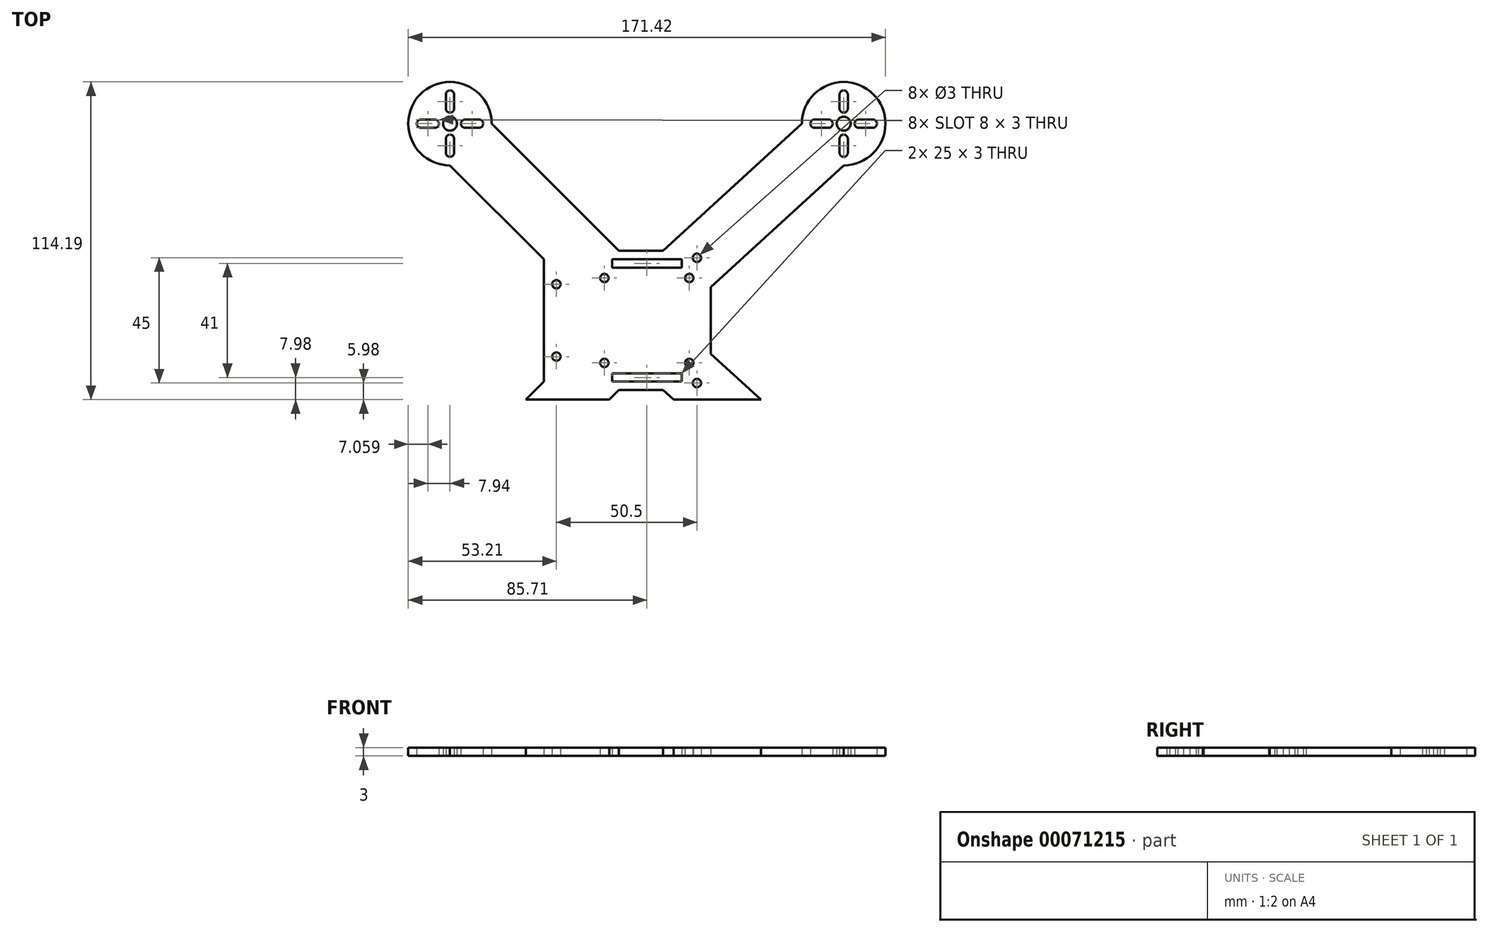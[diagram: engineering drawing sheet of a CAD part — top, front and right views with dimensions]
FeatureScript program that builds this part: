
annotation { "Feature Type Name" : "Feature", "Feature Type Description" : "" }
export const myFeature = defineFeature(function(context is Context, id is Id, definition is map)
    precondition{}
    {
        {
            var Q0;
            Q0=qCreatedBy(makeId("Top.planeOp"),FACE);
            var sketch = newSketch(context, id + "F0", { "sketchPlane" : qUnion([Q0])});
            skLineSegment(sketch, "E0.rect.left", {"start": v(70.71, -70.71) * mm, "end": v(70.71, 70.71) * mm, "construction": true});
            skLineSegment(sketch, "E0.rect.right", {"start": v(-70.71, -70.71) * mm, "end": v(-70.71, 70.71) * mm, "construction": true});
            skPoint(sketch, "E0.rect.middle", {"position": v(0, 0) * mm});
            skArc(sketch, "E1", {"start": v(-55.71, 70.71) * mm, "mid": v(-81.32, 81.32) * mm, "end": v(-70.71, 55.71) * mm});
            skLineSegment(sketch, "E2", {"start": v(70.71, 70.71) * mm, "end": v(-70.71, -70.71) * mm, "construction": true});
            skLineSegment(sketch, "E3", {"start": v(70.71, -70.71) * mm, "end": v(-70.71, 70.71) * mm, "construction": true});
            skCircle(sketch, "E4", {"center": v(-70.71, 70.71) * mm, "radius": 2.5 * mm});
            skLineSegment(sketch, "E5.rect.left", {"start": v(-69.21, 76.15) * mm, "end": v(-69.21, 81.15) * mm});
            skLineSegment(sketch, "E5.rect.right", {"start": v(-72.21, 76.15) * mm, "end": v(-72.21, 81.15) * mm});
            skArc(sketch, "E6", {"start": v(-69.21, 81.15) * mm, "mid": v(-70.71, 82.65) * mm, "end": v(-72.21, 81.15) * mm});
            skArc(sketch, "E7", {"start": v(-72.21, 76.15) * mm, "mid": v(-70.71, 74.65) * mm, "end": v(-69.21, 76.15) * mm});
            skLineSegment(sketch, "E8", {"start": v(-70.71, 70.71) * mm, "end": v(70.71, 70.71) * mm, "construction": true});
            skCircle(sketch, "E9.MirrorC", {"center": v(70.71, 70.71) * mm, "radius": 2.5 * mm});
            skArc(sketch, "E10.MirrorC", {"start": v(55.71, 70.71) * mm, "mid": v(81.32, 81.32) * mm, "end": v(70.71, 55.71) * mm});
            skLineSegment(sketch, "E11.rect.bottom", {"start": v(18, 18) * mm, "end": v(-18, 18) * mm, "construction": true});
            skLineSegment(sketch, "E11.rect.top", {"start": v(18, -18) * mm, "end": v(-18, -18) * mm, "construction": true});
            skLineSegment(sketch, "E11.rect.left", {"start": v(18, 18) * mm, "end": v(18, -18) * mm, "construction": true});
            skLineSegment(sketch, "E11.rect.right", {"start": v(-18, 18) * mm, "end": v(-18, -18) * mm, "construction": true});
            skLineSegment(sketch, "E12.rect.top", {"start": v(-10, 25) * mm, "end": v(5.83, 25) * mm});
            skLineSegment(sketch, "E12.rect.left", {"start": v(-37, -22) * mm, "end": v(-37, 22) * mm});
            skCircle(sketch, "E13", {"center": v(18, -22.5) * mm, "radius": 1.5 * mm});
            skCircle(sketch, "E14.MirrorC", {"center": v(18, 22.5) * mm, "radius": 1.5 * mm});
            skLineSegment(sketch, "E15.MirrorCS", {"start": v(70.71, 55.71) * mm, "end": v(23, 12) * mm});
            skLineSegment(sketch, "E16.MirrorCS", {"start": v(55.71, 70.71) * mm, "end": v(5.83, 25) * mm});
            skLineSegment(sketch, "E17.MirrorCS", {"start": v(-70.71, 55.71) * mm, "end": v(-37, 22) * mm});
            skLineSegment(sketch, "E18.MirrorCS", {"start": v(-55.71, 70.71) * mm, "end": v(-10, 25) * mm});
            skCircle(sketch, "E19", {"center": v(-32.5, -13) * mm, "radius": 1.5 * mm});
            skCircle(sketch, "E20.MirrorC", {"center": v(-32.5, 13) * mm, "radius": 1.5 * mm});
            skLineSegment(sketch, "E21.trimOffspring", {"start": v(23, 12) * mm, "end": v(23, -12) * mm});
            skLineSegment(sketch, "E22.trimOffspring", {"start": v(-10, -25) * mm, "end": v(5.83, -25) * mm});
            skLineSegment(sketch, "E23", {"start": v(-70.71, 70.71) * mm, "end": v(-68.94, 72.48) * mm});
            skLineSegment(sketch, "E24", {"start": v(-70.71, 70.71) * mm, "end": v(-72.48, 68.94) * mm});
            skLineSegment(sketch, "E25.MirrorCS", {"start": v(-69.21, 65.27) * mm, "end": v(-69.21, 60.27) * mm});
            skArc(sketch, "E26.MirrorCS", {"start": v(-69.21, 60.27) * mm, "mid": v(-70.71, 58.77) * mm, "end": v(-72.21, 60.27) * mm});
            skLineSegment(sketch, "E27.MirrorCS", {"start": v(-72.21, 65.27) * mm, "end": v(-72.21, 60.27) * mm});
            skArc(sketch, "E28.MirrorCS", {"start": v(-72.21, 65.27) * mm, "mid": v(-70.71, 66.77) * mm, "end": v(-69.21, 65.27) * mm});
            skLineSegment(sketch, "E29.MirrorCS", {"start": v(-65.27, 69.21) * mm, "end": v(-60.27, 69.21) * mm});
            skArc(sketch, "E30.MirrorCS", {"start": v(-65.27, 72.21) * mm, "mid": v(-66.77, 70.71) * mm, "end": v(-65.27, 69.21) * mm});
            skLineSegment(sketch, "E31.MirrorCS", {"start": v(-65.27, 72.21) * mm, "end": v(-60.27, 72.21) * mm});
            skArc(sketch, "E32.MirrorCS", {"start": v(-60.27, 69.21) * mm, "mid": v(-58.77, 70.71) * mm, "end": v(-60.27, 72.21) * mm});
            skLineSegment(sketch, "E33.MirrorCS", {"start": v(-76.15, 69.21) * mm, "end": v(-81.15, 69.21) * mm});
            skArc(sketch, "E34.MirrorCS", {"start": v(-76.15, 69.21) * mm, "mid": v(-74.65, 70.71) * mm, "end": v(-76.15, 72.21) * mm});
            skLineSegment(sketch, "E35.MirrorCS", {"start": v(-76.15, 72.21) * mm, "end": v(-81.15, 72.21) * mm});
            skArc(sketch, "E36.MirrorCS", {"start": v(-81.15, 72.21) * mm, "mid": v(-82.65, 70.71) * mm, "end": v(-81.15, 69.21) * mm});
            skArc(sketch, "E37.MirrorCS", {"start": v(72.21, 76.15) * mm, "mid": v(70.71, 74.65) * mm, "end": v(69.21, 76.15) * mm});
            skArc(sketch, "E38.MirrorCS", {"start": v(69.21, 81.15) * mm, "mid": v(70.71, 82.65) * mm, "end": v(72.21, 81.15) * mm});
            skLineSegment(sketch, "E39.MirrorCS", {"start": v(69.21, 76.15) * mm, "end": v(69.21, 81.15) * mm});
            skLineSegment(sketch, "E40.MirrorCS", {"start": v(72.21, 76.15) * mm, "end": v(72.21, 81.15) * mm});
            skLineSegment(sketch, "E41.MirrorCS", {"start": v(65.27, 69.21) * mm, "end": v(60.27, 69.21) * mm});
            skArc(sketch, "E42.MirrorCS", {"start": v(76.15, 69.21) * mm, "mid": v(74.65, 70.71) * mm, "end": v(76.15, 72.21) * mm});
            skArc(sketch, "E43.MirrorCS", {"start": v(81.15, 72.21) * mm, "mid": v(82.65, 70.71) * mm, "end": v(81.15, 69.21) * mm});
            skArc(sketch, "E44.MirrorCS", {"start": v(60.27, 69.21) * mm, "mid": v(58.77, 70.71) * mm, "end": v(60.27, 72.21) * mm});
            skArc(sketch, "E45.MirrorCS", {"start": v(65.27, 72.21) * mm, "mid": v(66.77, 70.71) * mm, "end": v(65.27, 69.21) * mm});
            skLineSegment(sketch, "E46.MirrorCS", {"start": v(76.15, 72.21) * mm, "end": v(81.15, 72.21) * mm});
            skLineSegment(sketch, "E47.MirrorCS", {"start": v(65.27, 72.21) * mm, "end": v(60.27, 72.21) * mm});
            skLineSegment(sketch, "E48.MirrorCS", {"start": v(76.15, 69.21) * mm, "end": v(81.15, 69.21) * mm});
            skLineSegment(sketch, "E49.MirrorCS", {"start": v(69.21, 65.27) * mm, "end": v(69.21, 60.27) * mm});
            skArc(sketch, "E50.MirrorCS", {"start": v(69.21, 60.27) * mm, "mid": v(70.71, 58.77) * mm, "end": v(72.21, 60.27) * mm});
            skArc(sketch, "E51.MirrorCS", {"start": v(72.21, 65.27) * mm, "mid": v(70.71, 66.77) * mm, "end": v(69.21, 65.27) * mm});
            skLineSegment(sketch, "E52.MirrorCS", {"start": v(72.21, 65.27) * mm, "end": v(72.21, 60.27) * mm});
            skCircle(sketch, "E53", {"center": v(-15.25, 15.25) * mm, "radius": 1.5 * mm});
            skCircle(sketch, "E54.MirrorC", {"center": v(15.25, 15.25) * mm, "radius": 1.5 * mm});
            skCircle(sketch, "E55.MirrorC", {"center": v(-15.25, -15.25) * mm, "radius": 1.5 * mm});
            skCircle(sketch, "E56.MirrorC", {"center": v(15.25, -15.25) * mm, "radius": 1.5 * mm});
            skLineSegment(sketch, "E57.rect.bottom", {"start": v(-12.5, 22) * mm, "end": v(12.5, 22) * mm});
            skLineSegment(sketch, "E57.rect.top", {"start": v(-12.5, 19) * mm, "end": v(12.5, 19) * mm});
            skLineSegment(sketch, "E57.rect.left", {"start": v(-12.5, 22) * mm, "end": v(-12.5, 19) * mm});
            skLineSegment(sketch, "E57.rect.right", {"start": v(12.5, 22) * mm, "end": v(12.5, 19) * mm});
            skPoint(sketch, "E57.rect.middle", {"position": v(0, 20.5) * mm});
            skPoint(sketch, "E58.MirrorP", {"position": v(0, -20.5) * mm});
            skLineSegment(sketch, "E59.MirrorCS", {"start": v(-12.5, -19) * mm, "end": v(12.5, -19) * mm});
            skLineSegment(sketch, "E60.MirrorCS", {"start": v(-12.5, -22) * mm, "end": v(-12.5, -19) * mm});
            skLineSegment(sketch, "E61.MirrorCS", {"start": v(-12.5, -22) * mm, "end": v(12.5, -22) * mm});
            skLineSegment(sketch, "E62.MirrorCS", {"start": v(12.5, -22) * mm, "end": v(12.5, -19) * mm});
            skLineSegment(sketch, "E63", {"start": v(-10, -25) * mm, "end": v(-13.48, -28.48) * mm});
            skLineSegment(sketch, "E64", {"start": v(-37, -22) * mm, "end": v(-43.48, -28.48) * mm});
            skLineSegment(sketch, "E65", {"start": v(5.83, -25) * mm, "end": v(9.62, -28.48) * mm});
            skLineSegment(sketch, "E66", {"start": v(23, -12) * mm, "end": v(41, -28.48) * mm});
            skLineSegment(sketch, "E67", {"start": v(-43.48, -28.48) * mm, "end": v(-13.48, -28.48) * mm});
            skLineSegment(sketch, "E68", {"start": v(9.62, -28.48) * mm, "end": v(41, -28.48) * mm});
            skSolve(sketch);
        }
        {
            var Q0;
            Q0=makeQuery(id+"F0.imprint","IMPRINT",FACE,{"disambiguationData":[TD([[makeQuery(id+"F0.imprint","IMPRINT",EDGE,{"derivedFrom":sQuery(id+"F0.wireOp",EDGE,"E1")}),1.0]])]});
            extrude(context, id + "F1", {"entities" : qUnion([Q0]), "depth" : 3 * mm});
        }
    });
